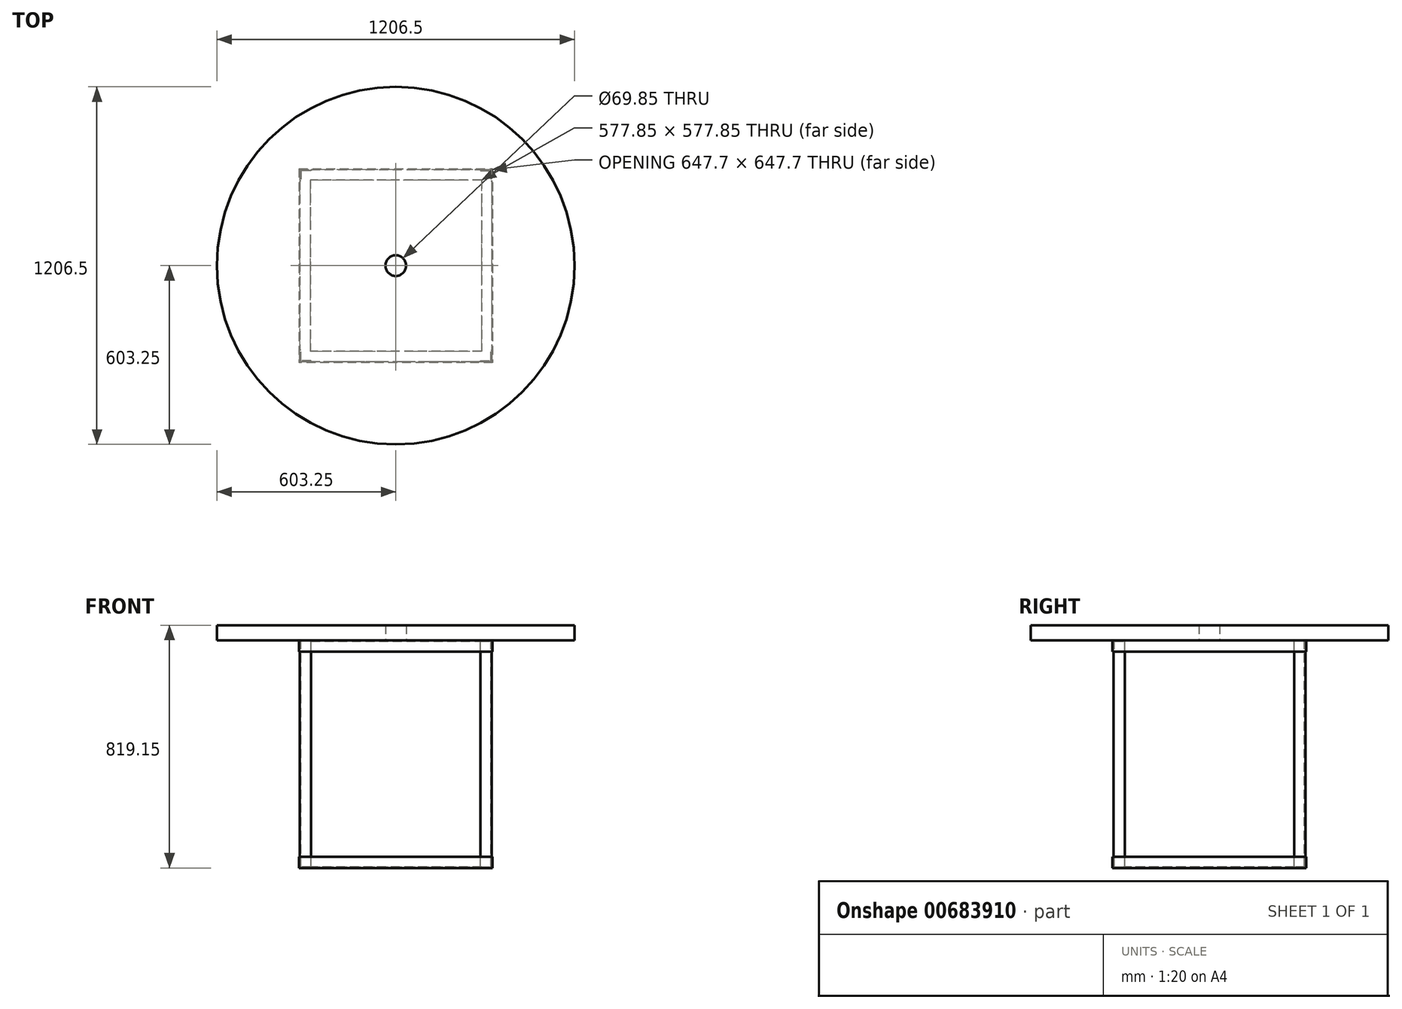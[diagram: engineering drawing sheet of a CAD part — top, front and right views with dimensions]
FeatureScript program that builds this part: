
annotation { "Feature Type Name" : "Feature", "Feature Type Description" : "" }
export const myFeature = defineFeature(function(context is Context, id is Id, definition is map)
    precondition{}
    {
        {
            var Q0;
            Q0=qCreatedBy(makeId("Top.planeOp"),FACE);
            var sketch = newSketch(context, id + "F0", { "sketchPlane" : qUnion([Q0])});
            skCircle(sketch, "E0", {"center": v(0, 0) * mm, "radius": 34.93 * mm});
            skCircle(sketch, "E1", {"center": v(0, 0) * mm, "radius": 603.25 * mm});
            skSolve(sketch);
        }
        {
            var Q0;
            Q0=makeQuery(id+"F0.imprint","IMPRINT",FACE,{"disambiguationData":[TD([[makeQuery(id+"F0.imprint","IMPRINT",EDGE,{"derivedFrom":sQuery(id+"F0.wireOp",EDGE,"E0")}),-1.0]])]});
            extrude(context, id + "F1", {"entities" : qUnion([Q0]), "depth" : 50.8 * mm, "offsetDistance" : 25.4 * mm});
        }
        {
            var Q0;
            Q0=makeQuery(id+"F1.opExtrude","CAP_FACE",FACE,{"disambiguationData":[OSD([sQuery(id+"F0.wireOp",EDGE,"E0"),sQuery(id+"F0.wireOp",EDGE,"E1")])],"isStart":true});
            var sketch = newSketch(context, id + "F2", { "sketchPlane" : qUnion([Q0])});
            skLineSegment(sketch, "E2.top", {"start": v(327.02, 327.03) * mm, "end": v(-327.03, 327.02) * mm});
            skLineSegment(sketch, "E2.left", {"start": v(327.03, -327.03) * mm, "end": v(327.03, 327.03) * mm});
            skLineSegment(sketch, "E2.right", {"start": v(-327.03, -327.03) * mm, "end": v(-327.03, 327.02) * mm});
            skLineSegment(sketch, "E3.bottom", {"start": v(288.93, -288.93) * mm, "end": v(-288.93, -288.93) * mm});
            skLineSegment(sketch, "E3.top", {"start": v(288.93, 288.92) * mm, "end": v(-288.93, 288.92) * mm});
            skLineSegment(sketch, "E3.left", {"start": v(288.93, -288.93) * mm, "end": v(288.93, 288.92) * mm});
            skLineSegment(sketch, "E3.right", {"start": v(-288.93, -288.93) * mm, "end": v(-288.93, 288.92) * mm});
            skPoint(sketch, "E4.end.orphan", {"position": v(-210.66, 288.92) * mm});
            skLineSegment(sketch, "E5", {"start": v(-327.03, -327.03) * mm, "end": v(327.03, -327.03) * mm});
            skSolve(sketch);
        }
        {
            var Q0;
            Q0=makeQuery(id+"F2.imprint","IMPRINT",FACE,{"disambiguationData":[TD([[makeQuery(id+"F2.imprint","IMPRINT",EDGE,{"derivedFrom":sQuery(id+"F2.wireOp",EDGE,"E2.top")}),1.0]])]});
            extrude(context, id + "F3", {"entities" : qUnion([Q0]), "operationType" : NewBodyOperationType.ADD, "depth" : 3.17 * mm, "offsetDistance" : 25.4 * mm});
        }
        {
            var Q0;
            Q0=makeQuery(id+"F3.opExtrude","CAP_FACE",FACE,{"disambiguationData":[OSD([sQuery(id+"F2.wireOp",EDGE,"E2.top"),sQuery(id+"F2.wireOp",EDGE,"E2.left"),sQuery(id+"F2.wireOp",EDGE,"E2.right"),sQuery(id+"F2.wireOp",EDGE,"E3.bottom"),sQuery(id+"F2.wireOp",EDGE,"E3.top"),sQuery(id+"F2.wireOp",EDGE,"E3.left"),sQuery(id+"F2.wireOp",EDGE,"E3.right"),sQuery(id+"F2.wireOp",EDGE,"E5")])],"isStart":false});
            var sketch = newSketch(context, id + "F4", { "sketchPlane" : qUnion([Q0])});
            skLineSegment(sketch, "E6.bottom", {"start": v(-323.85, -323.85) * mm, "end": v(323.85, -323.85) * mm});
            skLineSegment(sketch, "E6.top", {"start": v(-323.85, 323.85) * mm, "end": v(323.85, 323.85) * mm});
            skLineSegment(sketch, "E6.left", {"start": v(-323.85, -323.85) * mm, "end": v(-323.85, 323.85) * mm});
            skLineSegment(sketch, "E6.right", {"start": v(323.85, -323.85) * mm, "end": v(323.85, 323.85) * mm});
            skSolve(sketch);
        }
        {
            var Q0;
            Q0=makeQuery(id+"F4.imprint","IMPRINT",FACE,{"disambiguationData":[TD([[makeQuery(id+"F4.imprint","IMPRINT",EDGE,{"derivedFrom":sQuery(id+"F4.wireOp",EDGE,"E6.bottom")}),-1.0]])]});
            extrude(context, id + "F5", {"entities" : qUnion([Q0]), "operationType" : NewBodyOperationType.ADD, "depth" : 34.92 * mm, "offsetDistance" : 25.4 * mm});
        }
        {
            var Q0;
            Q0=makeQuery(id+"F3.opExtrude","CAP_FACE",FACE,{"disambiguationData":[OSD([sQuery(id+"F2.wireOp",EDGE,"E2.top"),sQuery(id+"F2.wireOp",EDGE,"E2.left"),sQuery(id+"F2.wireOp",EDGE,"E2.right"),sQuery(id+"F2.wireOp",EDGE,"E3.bottom"),sQuery(id+"F2.wireOp",EDGE,"E3.top"),sQuery(id+"F2.wireOp",EDGE,"E3.left"),sQuery(id+"F2.wireOp",EDGE,"E3.right"),sQuery(id+"F2.wireOp",EDGE,"E5")])],"isStart":false});
            var sketch = newSketch(context, id + "F6", { "sketchPlane" : qUnion([Q0])});
            skLineSegment(sketch, "E7", {"start": v(-323.85, 323.85) * mm, "end": v(-285.75, 323.85) * mm});
            skLineSegment(sketch, "E8", {"start": v(-285.75, 323.85) * mm, "end": v(-285.75, 320.68) * mm});
            skLineSegment(sketch, "E9", {"start": v(-285.75, 320.68) * mm, "end": v(-320.68, 320.68) * mm});
            skLineSegment(sketch, "E10", {"start": v(-320.68, 320.68) * mm, "end": v(-320.68, 285.75) * mm});
            skLineSegment(sketch, "E11", {"start": v(-320.68, 285.75) * mm, "end": v(-323.85, 285.75) * mm});
            skLineSegment(sketch, "E12", {"start": v(-323.85, 285.75) * mm, "end": v(-323.85, 323.85) * mm});
            skSolve(sketch);
        }
        {
            var Q0;
            Q0 = qSketchRegion(id + "F6", true);
            extrude(context, id + "F7", {"entities" : qUnion([Q0]), "operationType" : NewBodyOperationType.ADD, "depth" : 762 * mm, "offsetDistance" : 25.4 * mm});
        }
        {
            var Q0;
            Q0=makeQuery(id+"F3.opExtrude","CAP_FACE",FACE,{"disambiguationData":[OSD([sQuery(id+"F2.wireOp",EDGE,"E2.top"),sQuery(id+"F2.wireOp",EDGE,"E2.left"),sQuery(id+"F2.wireOp",EDGE,"E2.right"),sQuery(id+"F2.wireOp",EDGE,"E3.bottom"),sQuery(id+"F2.wireOp",EDGE,"E3.top"),sQuery(id+"F2.wireOp",EDGE,"E3.left"),sQuery(id+"F2.wireOp",EDGE,"E3.right"),sQuery(id+"F2.wireOp",EDGE,"E5")])],"isStart":false});
            var sketch = newSketch(context, id + "F8", { "sketchPlane" : qUnion([Q0])});
            skLineSegment(sketch, "E13", {"start": v(323.85, 323.85) * mm, "end": v(285.75, 323.85) * mm});
            skLineSegment(sketch, "E14", {"start": v(285.75, 323.85) * mm, "end": v(285.75, 320.68) * mm});
            skLineSegment(sketch, "E15", {"start": v(285.75, 320.68) * mm, "end": v(320.68, 320.68) * mm});
            skLineSegment(sketch, "E16", {"start": v(320.68, 320.68) * mm, "end": v(320.68, 285.75) * mm});
            skLineSegment(sketch, "E17", {"start": v(320.68, 285.75) * mm, "end": v(323.85, 285.75) * mm});
            skLineSegment(sketch, "E18", {"start": v(323.85, 285.75) * mm, "end": v(323.85, 323.85) * mm});
            skSolve(sketch);
        }
        {
            var Q0;
            Q0 = qSketchRegion(id + "F8", true);
            extrude(context, id + "F9", {"entities" : qUnion([Q0]), "operationType" : NewBodyOperationType.ADD, "depth" : 762 * mm, "offsetDistance" : 25.4 * mm});
        }
        {
            var Q0;
            Q0=makeQuery(id+"F3.opExtrude","CAP_FACE",FACE,{"disambiguationData":[OSD([sQuery(id+"F2.wireOp",EDGE,"E2.top"),sQuery(id+"F2.wireOp",EDGE,"E2.left"),sQuery(id+"F2.wireOp",EDGE,"E2.right"),sQuery(id+"F2.wireOp",EDGE,"E3.bottom"),sQuery(id+"F2.wireOp",EDGE,"E3.top"),sQuery(id+"F2.wireOp",EDGE,"E3.left"),sQuery(id+"F2.wireOp",EDGE,"E3.right"),sQuery(id+"F2.wireOp",EDGE,"E5")])],"isStart":false});
            var sketch = newSketch(context, id + "F10", { "sketchPlane" : qUnion([Q0])});
            skLineSegment(sketch, "E19", {"start": v(323.85, -323.85) * mm, "end": v(285.75, -323.85) * mm});
            skLineSegment(sketch, "E20", {"start": v(285.75, -323.85) * mm, "end": v(285.75, -320.68) * mm});
            skLineSegment(sketch, "E21", {"start": v(285.75, -320.68) * mm, "end": v(320.68, -320.68) * mm});
            skLineSegment(sketch, "E22", {"start": v(320.68, -320.68) * mm, "end": v(320.68, -285.75) * mm});
            skLineSegment(sketch, "E23", {"start": v(320.68, -285.75) * mm, "end": v(323.85, -285.75) * mm});
            skLineSegment(sketch, "E24", {"start": v(323.85, -285.75) * mm, "end": v(323.85, -323.85) * mm});
            skSolve(sketch);
        }
        {
            var Q0;
            Q0=makeQuery(id+"F10.imprint","IMPRINT",FACE,{"disambiguationData":[TD([[makeQuery(id+"F10.imprint","IMPRINT",EDGE,{"derivedFrom":sQuery(id+"F10.wireOp",EDGE,"E19")}),1.0]])]});
            extrude(context, id + "F11", {"entities" : qUnion([Q0]), "operationType" : NewBodyOperationType.ADD, "depth" : 762 * mm, "offsetDistance" : 25.4 * mm});
        }
        {
            var Q0;
            Q0=makeQuery(id+"F3.opExtrude","CAP_FACE",FACE,{"disambiguationData":[OSD([sQuery(id+"F2.wireOp",EDGE,"E2.top"),sQuery(id+"F2.wireOp",EDGE,"E2.left"),sQuery(id+"F2.wireOp",EDGE,"E2.right"),sQuery(id+"F2.wireOp",EDGE,"E3.bottom"),sQuery(id+"F2.wireOp",EDGE,"E3.top"),sQuery(id+"F2.wireOp",EDGE,"E3.left"),sQuery(id+"F2.wireOp",EDGE,"E3.right"),sQuery(id+"F2.wireOp",EDGE,"E5")])],"isStart":false});
            var sketch = newSketch(context, id + "F12", { "sketchPlane" : qUnion([Q0])});
            skLineSegment(sketch, "E25", {"start": v(-323.85, -323.85) * mm, "end": v(-285.75, -323.85) * mm});
            skLineSegment(sketch, "E26", {"start": v(-285.75, -323.85) * mm, "end": v(-285.75, -320.68) * mm});
            skLineSegment(sketch, "E27", {"start": v(-285.75, -320.68) * mm, "end": v(-320.68, -320.68) * mm});
            skLineSegment(sketch, "E28", {"start": v(-320.68, -320.68) * mm, "end": v(-320.68, -285.75) * mm});
            skLineSegment(sketch, "E29", {"start": v(-320.68, -285.75) * mm, "end": v(-323.85, -285.75) * mm});
            skLineSegment(sketch, "E30", {"start": v(-323.85, -285.75) * mm, "end": v(-323.85, -323.85) * mm});
            skSolve(sketch);
        }
        {
            var Q0;
            Q0=makeQuery(id+"F12.imprint","IMPRINT",FACE,{"disambiguationData":[TD([[makeQuery(id+"F12.imprint","IMPRINT",EDGE,{"derivedFrom":sQuery(id+"F12.wireOp",EDGE,"E25")}),1.0]])]});
            extrude(context, id + "F13", {"entities" : qUnion([Q0]), "operationType" : NewBodyOperationType.ADD, "depth" : 762 * mm, "offsetDistance" : 25.4 * mm});
        }
        {
            var Q0;
            Q0=makeQuery(id+"F9.opExtrude","CAP_FACE",FACE,{"disambiguationData":[OSD([sQuery(id+"F8.wireOp",EDGE,"E13"),sQuery(id+"F8.wireOp",EDGE,"E14"),sQuery(id+"F8.wireOp",EDGE,"E15"),sQuery(id+"F8.wireOp",EDGE,"E16"),sQuery(id+"F8.wireOp",EDGE,"E17"),sQuery(id+"F8.wireOp",EDGE,"E18")])],"isStart":false});
            var sketch = newSketch(context, id + "F14", { "sketchPlane" : qUnion([Q0])});
            skLineSegment(sketch, "E31", {"start": v(-323.85, -323.85) * mm, "end": v(-327.03, -323.85) * mm});
            skLineSegment(sketch, "E32", {"start": v(323.85, 323.85) * mm, "end": v(327.03, 323.85) * mm});
            skLineSegment(sketch, "E33", {"start": v(323.85, 323.85) * mm, "end": v(323.85, 327.03) * mm});
            skLineSegment(sketch, "E34", {"start": v(-323.85, -323.85) * mm, "end": v(-323.85, -327.03) * mm});
            skLineSegment(sketch, "E35.bottom", {"start": v(-327.03, -327.03) * mm, "end": v(327.03, -327.03) * mm});
            skLineSegment(sketch, "E35.top", {"start": v(-327.03, 327.03) * mm, "end": v(327.03, 327.03) * mm});
            skLineSegment(sketch, "E35.left", {"start": v(-327.03, -327.03) * mm, "end": v(-327.03, 327.03) * mm});
            skLineSegment(sketch, "E35.right", {"start": v(327.03, -327.03) * mm, "end": v(327.03, 327.03) * mm});
            skLineSegment(sketch, "E36.bottom", {"start": v(-323.85, 323.85) * mm, "end": v(323.85, 323.85) * mm});
            skLineSegment(sketch, "E36.top", {"start": v(-323.85, -323.85) * mm, "end": v(323.85, -323.85) * mm});
            skLineSegment(sketch, "E36.left", {"start": v(-323.85, 323.85) * mm, "end": v(-323.85, -323.85) * mm});
            skLineSegment(sketch, "E36.right", {"start": v(323.85, 323.85) * mm, "end": v(323.85, -323.85) * mm});
            skSolve(sketch);
        }
        {
            var Q0;
            Q0 = qSketchRegion(id + "F14", true);
            extrude(context, id + "F15", {"entities" : qUnion([Q0]), "operationType" : NewBodyOperationType.ADD, "oppositeDirection" : true, "depth" : 34.92 * mm, "offsetDistance" : 25.4 * mm});
        }
        {
            var Q0;
            Q0=makeQuery(id+"F15.boolean.opBoolean","MERGE",FACE,{"derivedFrom":[makeQuery(id+"F7.opExtrude","CAP_FACE",FACE,{"disambiguationData":[OSD([sQuery(id+"F6.wireOp",EDGE,"E7"),sQuery(id+"F6.wireOp",EDGE,"E8"),sQuery(id+"F6.wireOp",EDGE,"E9"),sQuery(id+"F6.wireOp",EDGE,"E10"),sQuery(id+"F6.wireOp",EDGE,"E11"),sQuery(id+"F6.wireOp",EDGE,"E12")])],"isStart":false}),makeQuery(id+"F9.opExtrude","CAP_FACE",FACE,{"disambiguationData":[OSD([sQuery(id+"F8.wireOp",EDGE,"E13"),sQuery(id+"F8.wireOp",EDGE,"E14"),sQuery(id+"F8.wireOp",EDGE,"E15"),sQuery(id+"F8.wireOp",EDGE,"E16"),sQuery(id+"F8.wireOp",EDGE,"E17"),sQuery(id+"F8.wireOp",EDGE,"E18")])],"isStart":false}),makeQuery(id+"F11.opExtrude","CAP_FACE",FACE,{"disambiguationData":[OSD([sQuery(id+"F10.wireOp",EDGE,"E19"),sQuery(id+"F10.wireOp",EDGE,"E20"),sQuery(id+"F10.wireOp",EDGE,"E21"),sQuery(id+"F10.wireOp",EDGE,"E22"),sQuery(id+"F10.wireOp",EDGE,"E23"),sQuery(id+"F10.wireOp",EDGE,"E24")])],"isStart":false}),makeQuery(id+"F13.opExtrude","CAP_FACE",FACE,{"disambiguationData":[OSD([sQuery(id+"F12.wireOp",EDGE,"E25"),sQuery(id+"F12.wireOp",EDGE,"E26"),sQuery(id+"F12.wireOp",EDGE,"E27"),sQuery(id+"F12.wireOp",EDGE,"E28"),sQuery(id+"F12.wireOp",EDGE,"E29"),sQuery(id+"F12.wireOp",EDGE,"E30")])],"isStart":false}),makeQuery(id+"F15.opExtrude","CAP_FACE",FACE,{"disambiguationData":[OSD([sQuery(id+"F14.wireOp",EDGE,"E35.bottom"),sQuery(id+"F14.wireOp",EDGE,"E35.top"),sQuery(id+"F14.wireOp",EDGE,"E35.left"),sQuery(id+"F14.wireOp",EDGE,"E35.right"),sQuery(id+"F14.wireOp",EDGE,"E36.bottom"),sQuery(id+"F14.wireOp",EDGE,"E36.top"),sQuery(id+"F14.wireOp",EDGE,"E36.left"),sQuery(id+"F14.wireOp",EDGE,"E36.right")])],"isStart":true})]});
            var sketch = newSketch(context, id + "F16", { "sketchPlane" : qUnion([Q0])});
            skLineSegment(sketch, "E37", {"start": v(-327.03, -327.03) * mm, "end": v(-327.03, -288.93) * mm});
            skLineSegment(sketch, "E38", {"start": v(-327.03, -327.03) * mm, "end": v(327.03, -327.03) * mm});
            skLineSegment(sketch, "E39", {"start": v(327.03, -327.03) * mm, "end": v(327.03, -288.93) * mm});
            skLineSegment(sketch, "E40", {"start": v(288.93, -288.93) * mm, "end": v(-288.93, -288.93) * mm});
            skLineSegment(sketch, "E41", {"start": v(-327.03, -288.93) * mm, "end": v(-327.03, 327.03) * mm});
            skLineSegment(sketch, "E42", {"start": v(-288.93, -288.93) * mm, "end": v(-288.93, 288.93) * mm});
            skLineSegment(sketch, "E43", {"start": v(-288.93, 327.03) * mm, "end": v(327.03, 327.03) * mm});
            skLineSegment(sketch, "E44", {"start": v(288.93, 288.93) * mm, "end": v(-288.93, 288.93) * mm});
            skLineSegment(sketch, "E45", {"start": v(-288.93, 327.03) * mm, "end": v(-327.03, 327.03) * mm});
            skLineSegment(sketch, "E46", {"start": v(327.03, 327.03) * mm, "end": v(288.93, 327.03) * mm});
            skLineSegment(sketch, "E47", {"start": v(327.03, -327.03) * mm, "end": v(288.93, -327.03) * mm});
            skLineSegment(sketch, "E48", {"start": v(288.93, -288.93) * mm, "end": v(288.93, 288.93) * mm});
            skLineSegment(sketch, "E49", {"start": v(327.03, 327.03) * mm, "end": v(327.03, -288.93) * mm});
            skSolve(sketch);
        }
        {
            var Q0;
            Q0 = qSketchRegion(id + "F16", true);
            extrude(context, id + "F17", {"entities" : qUnion([Q0]), "operationType" : NewBodyOperationType.ADD, "depth" : 3.17 * mm, "offsetDistance" : 25.4 * mm});
        }
    });
